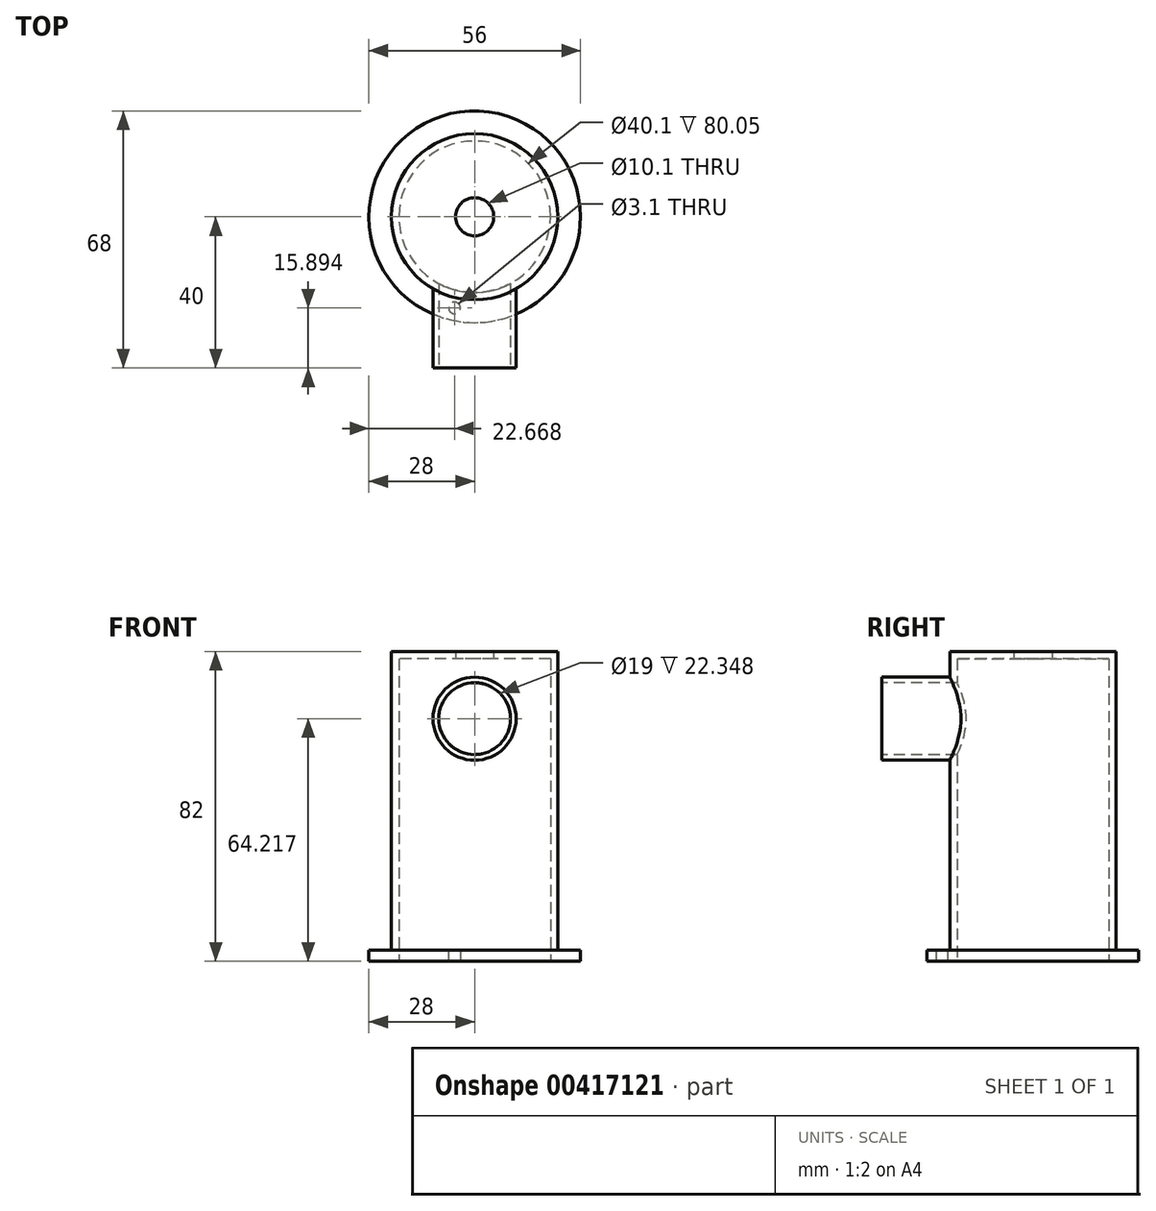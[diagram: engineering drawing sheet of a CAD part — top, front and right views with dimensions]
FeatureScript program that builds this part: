
annotation { "Feature Type Name" : "Feature", "Feature Type Description" : "" }
export const myFeature = defineFeature(function(context is Context, id is Id, definition is map)
    precondition{}
    {
        {
            var Q0;
            Q0=qCreatedBy(makeId("Top.planeOp"),FACE);
            var sketch = newSketch(context, id + "F0", { "sketchPlane" : qUnion([Q0])});
            skCircle(sketch, "E0", {"center": v(0, 0) * mm, "radius": 22 * mm});
            skCircle(sketch, "E1", {"center": v(0, 0) * mm, "radius": 28 * mm});
            skSolve(sketch);
        }
        {
            var Q0;
            Q0=makeQuery(id+"F0.imprint","IMPRINT",FACE,{"disambiguationData":[TD([[makeQuery(id+"F0.imprint","IMPRINT",EDGE,{"derivedFrom":sQuery(id+"F0.wireOp",EDGE,"E0")}),1.0]])]});
            extrude(context, id + "F1", {"entities" : qUnion([Q0]), "depth" : 82 * mm});
        }
        {
            var Q0;
            Q0=makeQuery(id+"F1.opExtrude","CAP_FACE",FACE,{"disambiguationData":[OSD([sQuery(id+"F0.wireOp",EDGE,"E0")])],"isStart":true});
            shell(context, id + "F2", {"entities" : qUnion([Q0]), "thickness" : 1.95 * mm});
        }
        {
            var Q0;
            Q0=makeQuery(id+"F0.imprint","IMPRINT",FACE,{"disambiguationData":[TD([[makeQuery(id+"F0.imprint","IMPRINT",EDGE,{"derivedFrom":sQuery(id+"F0.wireOp",EDGE,"E0")}),-1.0]])]});
            extrude(context, id + "F3", {"entities" : qUnion([Q0]), "operationType" : NewBodyOperationType.ADD, "depth" : 3 * mm});
        }
        {
            var Q0;
            Q0=qCreatedBy(makeId("Front.planeOp"),FACE);
            var sketch = newSketch(context, id + "F4", { "sketchPlane" : qUnion([Q0])});
            skLineSegment(sketch, "E2", {"start": v(0, -30.48) * mm, "end": v(0, 118.91) * mm, "construction": true});
            skSolve(sketch);
        }
        {
            var Q0;
            Q0=qCreatedBy(makeId("Top.planeOp"),FACE);
            var sketch = newSketch(context, id + "F5", { "sketchPlane" : qUnion([Q0])});
            skCircle(sketch, "E3", {"center": v(0, 0) * mm, "radius": 5.05 * mm});
            skSolve(sketch);
        }
        {
            var Q0;
            Q0=qSketchRegion(id+"F5",true);
            extrude(context, id + "F6", {"entities" : qUnion([Q0]), "operationType" : NewBodyOperationType.REMOVE, "depth" : 90 * mm});
        }
        {
            var Q0;
            Q0=makeQuery(id+"F0.imprint","IMPRINT",FACE,{"disambiguationData":[TD([[makeQuery(id+"F0.imprint","IMPRINT",EDGE,{"derivedFrom":sQuery(id+"F0.wireOp",EDGE,"E0")}),-1.0]])]});
            var sketch = newSketch(context, id + "F7", { "sketchPlane" : qUnion([Q0])});
            skCircle(sketch, "E4", {"center": v(-5.33, -24.1) * mm, "radius": 1.55 * mm});
            skSolve(sketch);
        }
        {
            var Q0;
            Q0=qSketchRegion(id+"F7",true);
            extrude(context, id + "F8", {"entities" : qUnion([Q0]), "operationType" : NewBodyOperationType.REMOVE, "depth" : 5 * mm});
        }
        {
            var Q0;
            Q0=qCreatedBy(makeId("Front.planeOp"),FACE);
            cPlane(context, id + "F9", {"entities" : qUnion([Q0]), "cplaneType" : CPlaneType.OFFSET, "offset" : 40 * mm, "width" : 150 * mm, "height" : 150 * mm});
        }
        {
            var Q0;
            Q0=qCreatedBy(id+"F9.planeOp",FACE);
            var sketch = newSketch(context, id + "F10", { "sketchPlane" : qUnion([Q0])});
            skCircle(sketch, "E5", {"center": v(0, 64.22) * mm, "radius": 11 * mm});
            skSolve(sketch);
        }
        {
            var Q0;
            Q0=makeQuery(id+"F10.imprint","IMPRINT",FACE,{"disambiguationData":[TD([[makeQuery(id+"F10.imprint","IMPRINT",EDGE,{"derivedFrom":sQuery(id+"F10.wireOp",EDGE,"E5")}),1.0]])]});
            extrude(context, id + "F11", {"entities" : qUnion([Q0]), "operationType" : NewBodyOperationType.ADD, "endBound" : BoundingType.UP_TO_NEXT, "oppositeDirection" : true, "depth" : 25 * mm});
        }
        {
            var Q0;
            Q0=makeQuery(id+"F11.opExtrude","CAP_FACE",FACE,{"disambiguationData":[OSD([sQuery(id+"F10.wireOp",EDGE,"E5")])],"isStart":true});
            var sketch = newSketch(context, id + "F12", { "sketchPlane" : qUnion([Q0])});
            skCircle(sketch, "E6", {"center": v(0, 64.22) * mm, "radius": 9.5 * mm});
            skSolve(sketch);
        }
        {
            var Q0;
            Q0=qSketchRegion(id+"F12",true);
            extrude(context, id + "F13", {"entities" : qUnion([Q0]), "operationType" : NewBodyOperationType.REMOVE, "oppositeDirection" : true, "depth" : 30 * mm});
        }
    });
